# Revit family: 2100.112 Rainhead Overflow Sump 650x430x390
name_source: partatom
category: Plumbing Fixtures
revit_build: Autodesk Revit 2016 (Build: 20150714_1515(x64)
units: mm (PartAtom-declared; Revit-internal decimal feet)

## family parameters
Always vertical = No
Cut with Voids When Loaded = No
OmniClass Number = 23.60.30.11
OmniClass Title = Pipework Products for General Use
Part Type = Normal
Room Calculation Point = No
Round Connector Dimension = Use Diameter
Shared = No
Work Plane-Based = No

## types (2) — shared parameters
CW Connection = No
CutOut Length = 520 mm  [stored 1.70604 ft]
CutOut Width = 305 mm  [stored 1.00066 ft]
DVW150 Nozzle Heigth = 314 mm  [stored 1.03018 ft]
DWV100 Nozzle Height = 389 mm  [stored 1.27625 ft]
Flow = 0.0 L/s
HW Connection = No
Left Edge Position = 240 mm  [stored 0.787402 ft]
Left Edge Void Position = 237 mm  [stored 0.777559 ft]
Length = 647 mm  [stored 2.1227 ft]
Manufacturer = Aquanight Industries Ltd
Material = Aquanight-Black
Model = 2100.114
Nozzles Distance = 242 mm  [stored 0.793963 ft]
Pool Depth = 249 mm  [stored 0.816929 ft]
Right Edge Position = 119 mm  [stored 0.39042 ft]
Right Edge Void Position = 116 mm  [stored 0.380577 ft]
URL = www.aquaknight.co.nz
Vent Connection = No
Waste Connection = Yes
Width = 433 mm
zero-valued in all types: Left Tube End

## per-type parameters (varying)
| type | Connector Diameter | Connector Location | Description |
| DWV175 | 175 mm  [stored 0.574147 ft] | 282 mm | Membrane Rainhead 650x430x390 DWV175 DN175 |
| DWV150 | 150 mm | 352 mm | Membrane Rainhead 650x430x390 DWV150 DN150 |

note: column(s) folded — value = type name in every type: Connector Description

note: [stored X ft] marks values corroborated as IEEE doubles in the binary element streams (Revit-internal decimal feet)

## geometry (parser evidence)
native form markers: Sweep x2
no freeform markers — native parametric forms only
